# Revit family: Shower-Handshower-KOHLER-Awaken-K-72420
name_source: partatom
category: Plumbing Fixtures
revit_build: Autodesk Revit 2015 (Build: 20140606_1530(x64)
units: mm (PartAtom-declared; Revit-internal decimal feet)

## types (5) — shared parameters
ADA Compliant = No
Assembly Code = D2010700
CW Connection = No
Cold Water Inlet = Cold Water Inlet
Date Modified = 5/14/2019
Default Elevation = 0"
Drain Included = No
Flow Rate = 2 GPM
HW Connection = Yes
Height = 9 11/16"
Hot Water Inlet = Hot Water Inlet
Length = 2 7/8"
Manufacturer = KOHLER Co.
MasterFormat 1995 = 15410
MasterFormat 2004 = 22.41.23
Material = Premium Metal Construction
Pressure = 0.00 psi
Product Documentation Link = https://www.us.kohler.com
Product Name = Awaken
Product Page URL = http://www.us.kohler.com
Tempered Water Inlet = Tempered Water Inlet
URL = https://www.us.kohler.com
Vent Connection = No
Waste Connection = No
Waste Water Outlet = Waste Water Outlet
WaterSense Certified = Yes
Width = 3 13/16"

## per-type parameters (varying)
| type | Description | Finish | Model | Type |
| 2 GPM,CP-Polished Chrome | B90 2.0 gpm multifunction handshower | Kohler-Metal-CP-Polished_Chrome | K-72420-CP | 1 |
| 2 GPM,BN-Vibrant Brushed Nickel | B90 2.0 gpm multifunction handshower | Kohler-Metal-BN-Vibrant_Brushed_Nickel | K-72420-BN | 2 |
| 1.75 GPM,BN-Vibrant Brushed Nickel | B90 1.75 gpm multifunction handshower | Kohler-Metal-BN-Vibrant_Brushed_Nickel | K-72420-G-BN | 4 |
| 1.75 GPM,CP-Polished Chrome | B90 1.75 gpm multifunction handshower | Kohler-Metal-CP-Polished_Chrome | K-72420-G-CP | 3 |
| 1.5 GPM,CP-Polished Chrome | B90 1.5 gpm multifunction handshower | Kohler-Metal-CP-Polished_Chrome | K-72420-H-CP | 5 |

## geometry (parser evidence)
native form markers: Sweep x6
no freeform markers — native parametric forms only
